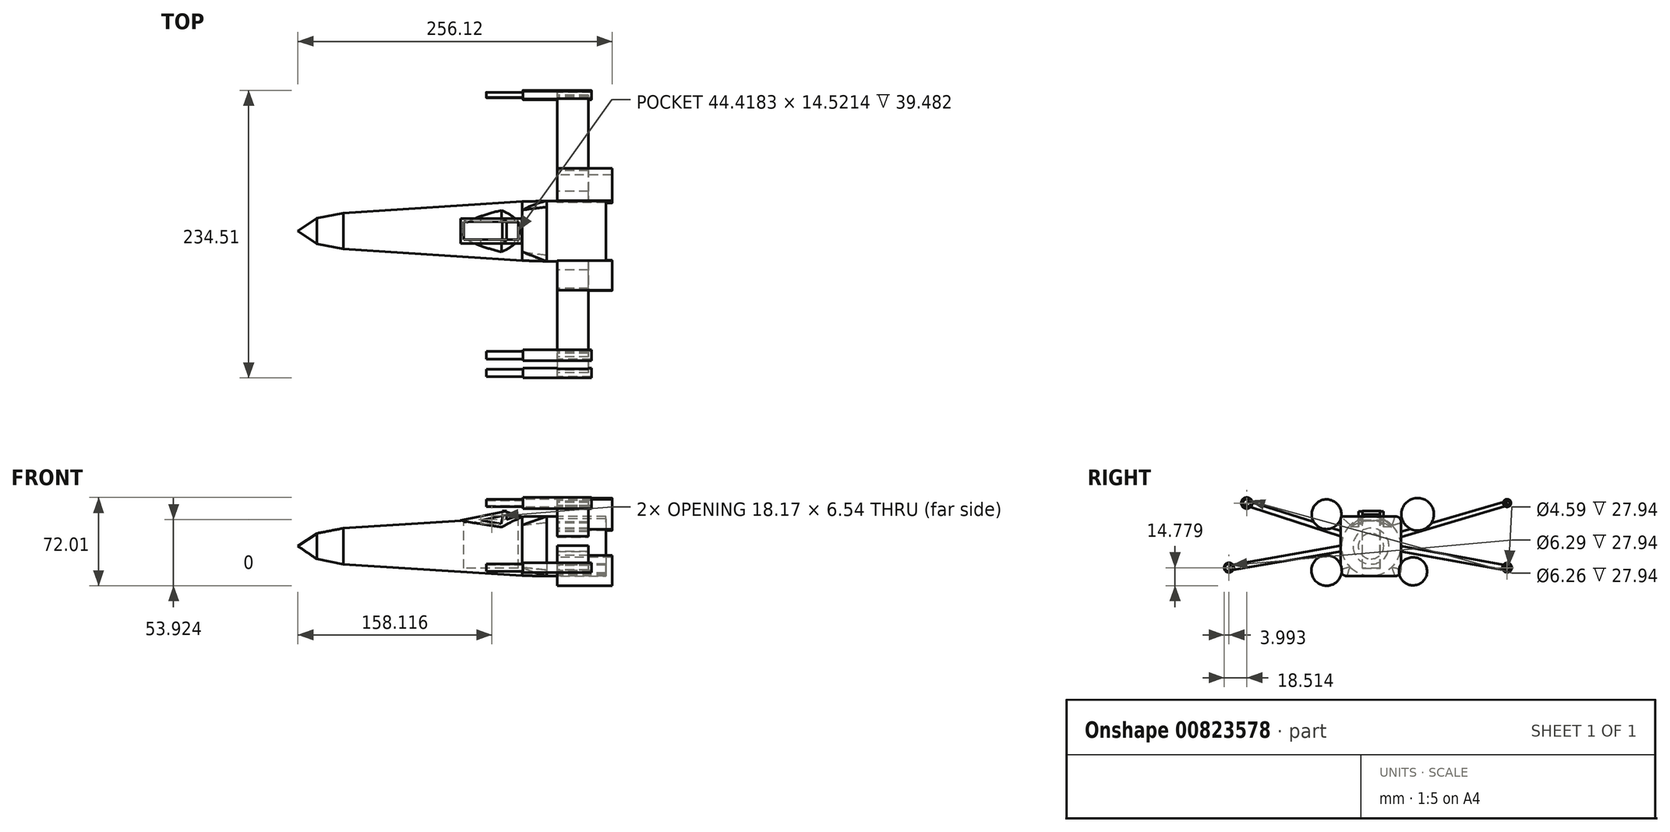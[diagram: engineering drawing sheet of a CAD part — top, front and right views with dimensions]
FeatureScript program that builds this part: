
annotation { "Feature Type Name" : "Feature", "Feature Type Description" : "" }
export const myFeature = defineFeature(function(context is Context, id is Id, definition is map)
    precondition{}
    {
        {
            var Q0;
            Q0=qCreatedBy(makeId("Front.planeOp"),FACE);
            var sketch = newSketch(context, id + "F0", { "sketchPlane" : qUnion([Q0])});
            skLineSegment(sketch, "E0", {"start": v(-58.23, 14.66) * mm, "end": v(-79.87, 10.4) * mm});
            skLineSegment(sketch, "E1", {"start": v(-95.24, 0) * mm, "end": v(0, 0) * mm});
            skLineSegment(sketch, "E2", {"start": v(-95.24, 0) * mm, "end": v(-79.87, 10.4) * mm});
            skPoint(sketch, "E3.start.orphan", {"position": v(0, 19.5) * mm});
            skLineSegment(sketch, "E4", {"start": v(-58.23, 14.66) * mm, "end": v(87.71, 24.06) * mm});
            skLineSegment(sketch, "E5", {"start": v(87.71, 24.06) * mm, "end": v(87.71, 0) * mm});
            skLineSegment(sketch, "E6", {"start": v(87.71, 0) * mm, "end": v(0, 0) * mm});
            skSolve(sketch);
        }
        {
            var Q0;
            Q0=makeQuery(id+"F0.imprint","IMPRINT",FACE,{"disambiguationData":[TD([[makeQuery(id+"F0.imprint","IMPRINT",EDGE,{"derivedFrom":sQuery(id+"F0.wireOp",EDGE,"E0")}),1.0]])]});
            var Q1;
            Q1=sQuery(id+"F0.wireOp",EDGE,"E1");
            revolve(context, id + "F1", {"surfaceOperationType" : NewSurfaceOperationType.NEW, "entities" : qUnion([Q0]), "axis" : qUnion([Q1]), "revolveType" : RevolveType.FULL});
        }
        {
            var Q0;
            Q0=qCreatedBy(makeId("Right.planeOp"),FACE);
            cPlane(context, id + "F2", {"entities" : qUnion([Q0]), "cplaneType" : CPlaneType.OFFSET, "offset" : 107.44 * mm, "width" : 152.4 * mm, "height" : 152.4 * mm});
        }
        {
            var Q0;
            Q0=qCreatedBy(id+"F2.planeOp",FACE);
            var sketch = newSketch(context, id + "F3", { "sketchPlane" : qUnion([Q0])});
            skLineSegment(sketch, "E7.bottom", {"start": v(24.63, 24.34) * mm, "end": v(-24.63, 24.34) * mm});
            skLineSegment(sketch, "E7.top", {"start": v(24.63, -24.34) * mm, "end": v(-24.63, -24.34) * mm});
            skLineSegment(sketch, "E7.left", {"start": v(24.63, 24.34) * mm, "end": v(24.63, -24.34) * mm});
            skLineSegment(sketch, "E7.right", {"start": v(-24.63, 24.34) * mm, "end": v(-24.63, -24.34) * mm});
            skPoint(sketch, "E7.middle", {"position": v(0, 0) * mm});
            skSolve(sketch);
        }
        {
            var Q1;
            Q1=makeQuery(id+"F1.opRevolve","SWEPT_FACE",FACE,{"disambiguationData":[OSD([sQuery(id+"F0.wireOp",EDGE,"E5")])]});
            var Q2;
            Q2=makeQuery(id+"F3.imprint","IMPRINT",FACE,{"disambiguationData":[TD([[makeQuery(id+"F3.imprint","IMPRINT",EDGE,{"derivedFrom":sQuery(id+"F3.wireOp",EDGE,"E7.bottom")}),1.0]])]});
            loft(context, id + "F4", {"operationType" : NewBodyOperationType.ADD, "sheetProfilesArray" : [{ "sheetProfileEntities" : qUnion([Q1]) }, { "sheetProfileEntities" : qUnion([Q2]) }]});
        }
        {
            var Q0;
            Q0=makeQuery(id+"F4.opLoft","SWEPT_EDGE",EDGE,{"disambiguationData":[OSD([sQuery(id+"F0.wireOp",EDGE,"E4"),sQuery(id+"F0.wireOp",EDGE,"E5"),sQuery(id+"F3.wireOp",EDGE,"E7.bottom"),sQuery(id+"F3.wireOp",EDGE,"E7.left"),sQuery(id+"F3.wireOp",EDGE,"E7.right")])]});
            var Q1;
            Q1=makeQuery(id+"F4.opLoft","SWEPT_EDGE",EDGE,{"disambiguationData":[OSD([sQuery(id+"F0.wireOp",EDGE,"E4"),sQuery(id+"F0.wireOp",EDGE,"E5"),sQuery(id+"F3.wireOp",EDGE,"E7.bottom"),sQuery(id+"F3.wireOp",EDGE,"E7.top"),sQuery(id+"F3.wireOp",EDGE,"E7.right")])]});
            var Q2;
            Q2=makeQuery(id+"F4.opLoft","SWEPT_EDGE",EDGE,{"disambiguationData":[OSD([sQuery(id+"F0.wireOp",EDGE,"E4"),sQuery(id+"F0.wireOp",EDGE,"E5"),sQuery(id+"F3.wireOp",EDGE,"E7.top"),sQuery(id+"F3.wireOp",EDGE,"E7.left"),sQuery(id+"F3.wireOp",EDGE,"E7.right")])]});
            var Q3;
            Q3=makeQuery(id+"F4.opLoft","SWEPT_EDGE",EDGE,{"disambiguationData":[OSD([sQuery(id+"F3.wireOp",EDGE,"E7.bottom"),sQuery(id+"F3.wireOp",EDGE,"E7.left")])]});
            fillet(context, id + "F5", {"entities" : qUnion([Q0, Q1, Q2, Q3]), "radius" : 5.08 * mm, "tangentPropagation" : true, "allowEdgeOverflow" : false});
        }
        {
            var Q0;
            Q0=qCreatedBy(makeId("Front.planeOp"),FACE);
            var sketch = newSketch(context, id + "F6", { "sketchPlane" : qUnion([Q0])});
            skLineSegment(sketch, "E8", {"start": v(35.57, 21.21) * mm, "end": v(70.6, 15.52) * mm});
            skLineSegment(sketch, "E9", {"start": v(70.6, 15.52) * mm, "end": v(87.96, 24.63) * mm});
            skLineSegment(sketch, "E10", {"start": v(87.96, 24.63) * mm, "end": v(70.6, 39.44) * mm});
            skLineSegment(sketch, "E11", {"start": v(65.18, 39.72) * mm, "end": v(35.57, 21.21) * mm});
            skLineSegment(sketch, "E12", {"start": v(65.18, 39.72) * mm, "end": v(70.6, 39.44) * mm});
            skSolve(sketch);
        }
        {
            var Q0;
            Q0 = qSketchRegion(id + "F6", true);
            extrude(context, id + "F7", {"entities" : qUnion([Q0]), "operationType" : NewBodyOperationType.REMOVE, "oppositeDirection" : true, "depth" : 49.78 * mm, "offsetDistance" : 25.4 * mm, "symmetric" : true});
        }
        {
            var Q0;
            Q0=qCreatedBy(makeId("Front.planeOp"),FACE);
            var sketch = newSketch(context, id + "F8", { "sketchPlane" : qUnion([Q0])});
            skLineSegment(sketch, "E13", {"start": v(37.28, 20.93) * mm, "end": v(73.72, 28.33) * mm});
            skLineSegment(sketch, "E14", {"start": v(73.72, 28.33) * mm, "end": v(87.1, 23.78) * mm});
            skLineSegment(sketch, "E15", {"start": v(87.1, 23.78) * mm, "end": v(70.3, 15.23) * mm});
            skLineSegment(sketch, "E16", {"start": v(70.3, 15.23) * mm, "end": v(37.28, 20.93) * mm});
            skLineSegment(sketch, "E17", {"start": v(70.3, 18.37) * mm, "end": v(53.8, 21.21) * mm});
            skPoint(sketch, "E17.endSnap0", {"position": v(53.8, 18.08) * mm});
            skLineSegment(sketch, "E18", {"start": v(53.8, 21.21) * mm, "end": v(71.96, 24.9) * mm});
            skLineSegment(sketch, "E19", {"start": v(71.96, 24.9) * mm, "end": v(70.3, 18.37) * mm});
            skLineSegment(sketch, "E20", {"start": v(74.86, 24.9) * mm, "end": v(74.86, 21.63) * mm});
            skPoint(sketch, "E20.endSnap0", {"position": v(71.13, 21.63) * mm});
            skLineSegment(sketch, "E21", {"start": v(74.86, 24.9) * mm, "end": v(81.4, 23.78) * mm});
            skLineSegment(sketch, "E22", {"start": v(81.4, 23.78) * mm, "end": v(74.86, 21.63) * mm});
            skSolve(sketch);
        }
        {
            var Q0;
            Q0=makeQuery(id+"F8.imprint","IMPRINT",FACE,{"disambiguationData":[TD([[makeQuery(id+"F8.imprint","IMPRINT",EDGE,{"derivedFrom":sQuery(id+"F8.wireOp",EDGE,"E13")}),-1.0]])]});
            extrude(context, id + "F9", {"entities" : qUnion([Q0]), "operationType" : NewBodyOperationType.ADD, "depth" : 20.32 * mm, "offsetDistance" : 25.4 * mm, "symmetric" : true});
        }
        {
            var Q0;
            Q0=qCreatedBy(makeId("Top.planeOp"),FACE);
            var sketch = newSketch(context, id + "F10", { "sketchPlane" : qUnion([Q0])});
            skLineSegment(sketch, "E23", {"start": v(39.84, 7.55) * mm, "end": v(39.84, -6.98) * mm});
            skLineSegment(sketch, "E24", {"start": v(39.84, -6.98) * mm, "end": v(84.26, -6.98) * mm});
            skLineSegment(sketch, "E25", {"start": v(84.26, -6.98) * mm, "end": v(84.26, 7.26) * mm});
            skLineSegment(sketch, "E26", {"start": v(84.26, 7.26) * mm, "end": v(39.84, 7.55) * mm});
            skSolve(sketch);
        }
        {
            var Q0;
            Q0 = qSketchRegion(id + "F10", true);
            extrude(context, id + "F11", {"entities" : qUnion([Q0]), "operationType" : NewBodyOperationType.REMOVE, "oppositeDirection" : true, "depth" : 36.07 * mm, "offsetDistance" : 25.4 * mm, "symmetric" : true});
        }
        {
            var Q0;
            Q0 = qSketchRegion(id + "F10", true);
            extrude(context, id + "F12", {"entities" : qUnion([Q0]), "operationType" : NewBodyOperationType.REMOVE, "depth" : 43.18 * mm, "offsetDistance" : 25.4 * mm});
        }
        {
            var Q0;
            Q0=qCreatedBy(makeId("Top.planeOp"),FACE);
            cPlane(context, id + "F13", {"entities" : qUnion([Q0]), "cplaneType" : CPlaneType.OFFSET, "offset" : 28.7 * mm, "width" : 152.4 * mm, "height" : 152.4 * mm});
        }
        {
            var Q0;
            Q0=qCreatedBy(id+"F13.planeOp",FACE);
            var sketch = newSketch(context, id + "F14", { "sketchPlane" : qUnion([Q0])});
            skLineSegment(sketch, "E27", {"start": v(71.45, 7.55) * mm, "end": v(71.45, -6.98) * mm});
            skLineSegment(sketch, "E28", {"start": v(74.86, 7.83) * mm, "end": v(74.86, -6.98) * mm});
            skLineSegment(sketch, "E29", {"start": v(74.86, -6.98) * mm, "end": v(71.45, -6.98) * mm});
            skLineSegment(sketch, "E30", {"start": v(71.45, 7.55) * mm, "end": v(74.86, 7.83) * mm});
            skSolve(sketch);
        }
        {
            var Q0;
            Q0 = qSketchRegion(id + "F14", true);
            extrude(context, id + "F15", {"entities" : qUnion([Q0]), "operationType" : NewBodyOperationType.ADD, "oppositeDirection" : true, "depth" : 2.8 * mm, "offsetDistance" : 25.4 * mm});
        }
        {
            var Q0;
            Q0=makeQuery(id+"F4.opLoft","CAP_FACE",FACE,{"disambiguationData":[OSD([makeQuery(id+"F3.imprint","IMPRINT",FACE,{"disambiguationData":[TD([[makeQuery(id+"F3.imprint","IMPRINT",EDGE,{"derivedFrom":sQuery(id+"F3.wireOp",EDGE,"E7.bottom")}),1.0]])]})])],"isStart":true});
            extrude(context, id + "F16", {"entities" : qUnion([Q0]), "operationType" : NewBodyOperationType.ADD, "depth" : 48.26 * mm, "offsetDistance" : 25.4 * mm});
        }
        {
            var Q0;
            Q0=qCreatedBy(id+"F2.planeOp",FACE);
            cPlane(context, id + "F17", {"entities" : qUnion([Q0]), "cplaneType" : CPlaneType.OFFSET, "offset" : 8.64 * mm, "width" : 152.4 * mm, "height" : 152.4 * mm});
        }
        {
            var Q0;
            Q0=qCreatedBy(id+"F17.planeOp",FACE);
            var sketch = newSketch(context, id + "F18", { "sketchPlane" : qUnion([Q0])});
            skLineSegment(sketch, "E31", {"start": v(0, 4.7) * mm, "end": v(110.05, 36.59) * mm});
            skLineSegment(sketch, "E32", {"start": v(110.05, 36.59) * mm, "end": v(111.02, 33.25) * mm});
            skLineSegment(sketch, "E33", {"start": v(111.02, 33.25) * mm, "end": v(0, 0) * mm});
            skLineSegment(sketch, "E34", {"start": v(0, 0) * mm, "end": v(0, 4.7) * mm});
            skLineSegment(sketch, "E35", {"start": v(0, 4.7) * mm, "end": v(111.02, -15.8) * mm});
            skLineSegment(sketch, "E36", {"start": v(111.02, -15.8) * mm, "end": v(110.3, -19.7) * mm});
            skLineSegment(sketch, "E37", {"start": v(110.3, -19.7) * mm, "end": v(0, 0) * mm});
            skLineSegment(sketch, "E38", {"start": v(0, 4.7) * mm, "end": v(-99.23, 36.59) * mm});
            skLineSegment(sketch, "E39", {"start": v(-99.23, 36.59) * mm, "end": v(-102.36, 33.25) * mm});
            skLineSegment(sketch, "E40", {"start": v(-102.36, 33.25) * mm, "end": v(0, 0) * mm});
            skLineSegment(sketch, "E41", {"start": v(0, 0) * mm, "end": v(-115.46, -19.7) * mm});
            skLineSegment(sketch, "E42", {"start": v(-115.46, -19.7) * mm, "end": v(-115.46, -15.8) * mm});
            skLineSegment(sketch, "E43", {"start": v(-115.46, -15.8) * mm, "end": v(0, 4.7) * mm});
            skSolve(sketch);
        }
        {
            var Q0;
            Q0 = qSketchRegion(id + "F18", true);
            extrude(context, id + "F19", {"entities" : qUnion([Q0]), "operationType" : NewBodyOperationType.ADD, "depth" : 25.4 * mm, "offsetDistance" : 25.4 * mm});
        }
        {
            var Q0;
            Q0=qCreatedBy(id+"F17.planeOp",FACE);
            var sketch = newSketch(context, id + "F20", { "sketchPlane" : qUnion([Q0])});
            skCircle(sketch, "E44", {"center": v(110.96, 35.16) * mm, "radius": 3.18 * mm});
            skCircle(sketch, "E45", {"center": v(110.96, -17.51) * mm, "radius": 3.87 * mm});
            skCircle(sketch, "E46", {"center": v(-115.69, -17.51) * mm, "radius": 4 * mm});
            skCircle(sketch, "E47", {"center": v(-101.17, 35.16) * mm, "radius": 4.56 * mm});
            skCircle(sketch, "E48", {"center": v(110.96, 35.16) * mm, "radius": 2 * mm});
            skCircle(sketch, "E49", {"center": v(110.96, -17.51) * mm, "radius": 2.3 * mm});
            skCircle(sketch, "E50", {"center": v(-115.69, -17.51) * mm, "radius": 3.14 * mm});
            skCircle(sketch, "E51", {"center": v(-101.17, 35.16) * mm, "radius": 3.13 * mm});
            skSolve(sketch);
        }
        {
            var Q0;
            Q0=makeQuery(id+"F20.imprint","IMPRINT",FACE,{"disambiguationData":[TD([[makeQuery(id+"F20.imprint","IMPRINT",EDGE,{"derivedFrom":sQuery(id+"F20.wireOp",EDGE,"E44")}),1.0]])]});
            var Q1;
            Q1=makeQuery(id+"F20.imprint","IMPRINT",FACE,{"disambiguationData":[TD([[makeQuery(id+"F20.imprint","IMPRINT",EDGE,{"derivedFrom":sQuery(id+"F20.wireOp",EDGE,"E45")}),1.0]])]});
            var Q2;
            Q2=makeQuery(id+"F20.imprint","IMPRINT",FACE,{"disambiguationData":[TD([[makeQuery(id+"F20.imprint","IMPRINT",EDGE,{"derivedFrom":sQuery(id+"F20.wireOp",EDGE,"E46")}),1.0]])]});
            var Q3;
            Q3=makeQuery(id+"F20.imprint","IMPRINT",FACE,{"disambiguationData":[TD([[makeQuery(id+"F20.imprint","IMPRINT",EDGE,{"derivedFrom":sQuery(id+"F20.wireOp",EDGE,"E47")}),1.0]])]});
            extrude(context, id + "F21", {"entities" : qUnion([Q0, Q1, Q2, Q3]), "operationType" : NewBodyOperationType.ADD, "depth" : 55.88 * mm, "offsetDistance" : 25.4 * mm, "symmetric" : true});
        }
        {
            var Q0;
            Q0=makeQuery(id+"F20.imprint","IMPRINT",FACE,{"disambiguationData":[TD([[makeQuery(id+"F20.imprint","IMPRINT",EDGE,{"derivedFrom":sQuery(id+"F20.wireOp",EDGE,"E51")}),1.0]])]});
            var Q1;
            Q1=makeQuery(id+"F20.imprint","IMPRINT",FACE,{"disambiguationData":[TD([[makeQuery(id+"F20.imprint","IMPRINT",EDGE,{"derivedFrom":sQuery(id+"F20.wireOp",EDGE,"E50")}),1.0]])]});
            var Q2;
            Q2=makeQuery(id+"F20.imprint","IMPRINT",FACE,{"disambiguationData":[TD([[makeQuery(id+"F20.imprint","IMPRINT",EDGE,{"derivedFrom":sQuery(id+"F20.wireOp",EDGE,"E48")}),1.0]])]});
            var Q3;
            Q3=makeQuery(id+"F20.imprint","IMPRINT",FACE,{"disambiguationData":[TD([[makeQuery(id+"F20.imprint","IMPRINT",EDGE,{"derivedFrom":sQuery(id+"F20.wireOp",EDGE,"E49")}),1.0]])]});
            extrude(context, id + "F22", {"entities" : qUnion([Q0, Q1, Q2, Q3]), "operationType" : NewBodyOperationType.ADD, "oppositeDirection" : true, "depth" : 57.74 * mm, "offsetDistance" : 25.4 * mm});
        }
        {
            var Q0;
            Q0=qCreatedBy(id+"F17.planeOp",FACE);
            var sketch = newSketch(context, id + "F23", { "sketchPlane" : qUnion([Q0])});
            skCircle(sketch, "E52", {"center": v(-36.21, 26.02) * mm, "radius": 12.12 * mm});
            skCircle(sketch, "E53", {"center": v(38.06, 26.02) * mm, "radius": 13.26 * mm});
            skPoint(sketch, "E54.center.orphan", {"position": v(-33.17, 0) * mm});
            skArc(sketch, "E55", {"start": v(-33.17, 0) * mm, "mid": v(-35.4, -9.84) * mm, "end": v(-36.21, -19.9) * mm});
            skPoint(sketch, "E55.second.point", {"position": v(-36.21, -19.9) * mm});
            skPoint(sketch, "E55.third.point", {"position": v(-36.21, -19.9) * mm});
            skCircle(sketch, "E56", {"center": v(-36.21, -19.9) * mm, "radius": 12.4 * mm});
            skCircle(sketch, "E57", {"center": v(34.3, -20.5) * mm, "radius": 11.46 * mm});
            skSolve(sketch);
        }
        {
            var Q0;
            Q0 = qSketchRegion(id + "F23", true);
            extrude(context, id + "F24", {"entities" : qUnion([Q0]), "operationType" : NewBodyOperationType.ADD, "depth" : 44.8 * mm, "offsetDistance" : 25.4 * mm});
        }
    });
